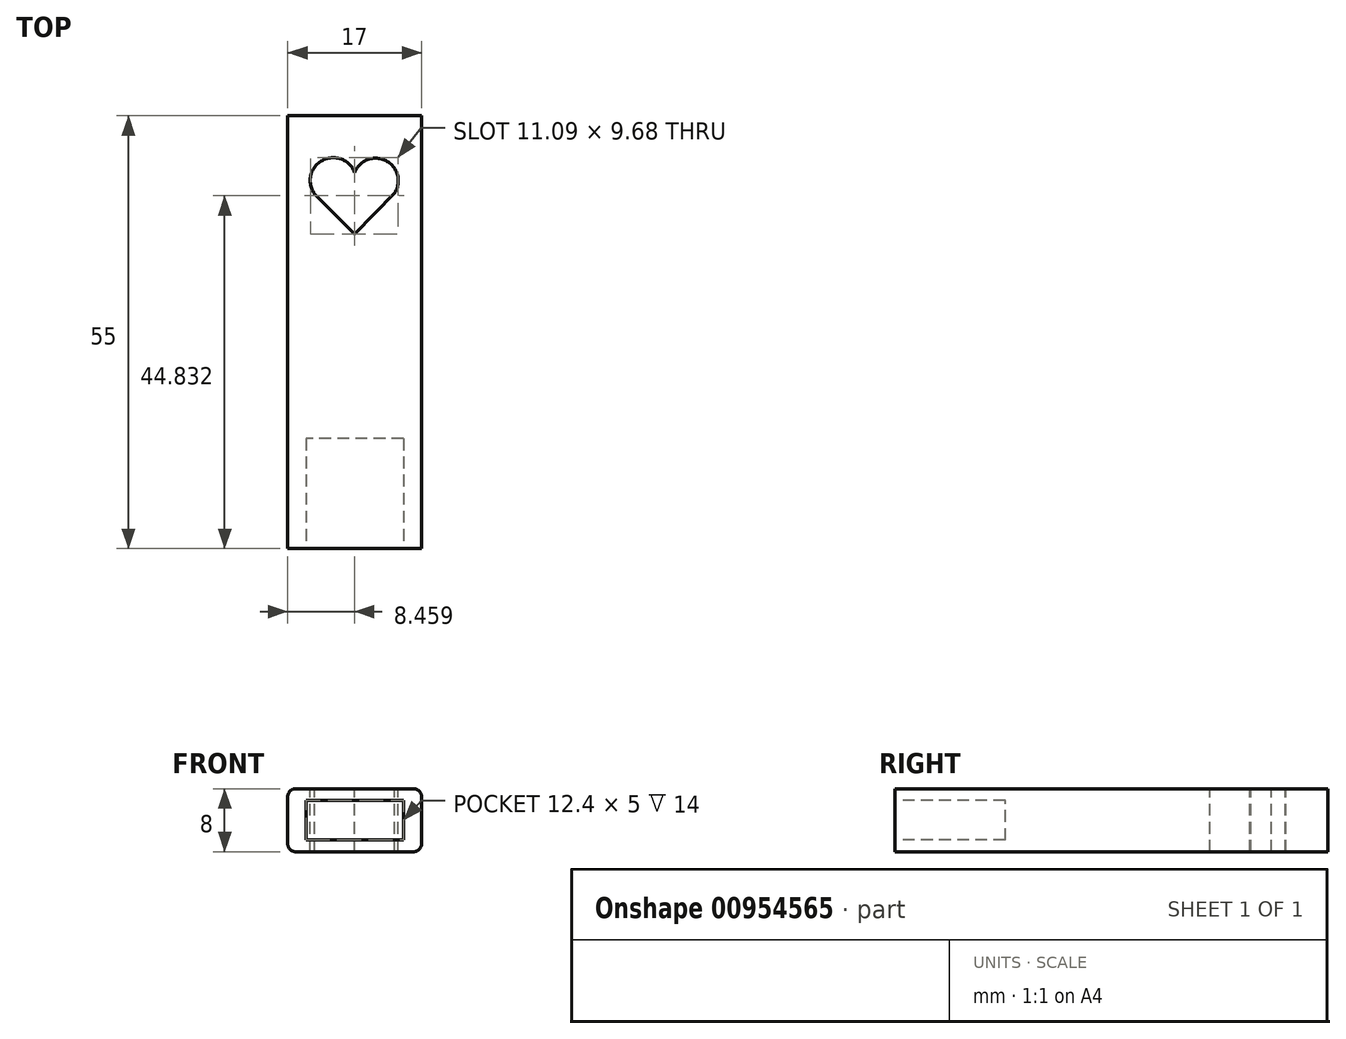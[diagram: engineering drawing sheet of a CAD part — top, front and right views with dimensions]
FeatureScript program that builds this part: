
annotation { "Feature Type Name" : "Feature", "Feature Type Description" : "" }
export const myFeature = defineFeature(function(context is Context, id is Id, definition is map)
    precondition{}
    {
        {
            var Q0;
            Q0=qCreatedBy(makeId("Front.planeOp"),FACE);
            var sketch = newSketch(context, id + "F0", { "sketchPlane" : qUnion([Q0])});
            skLineSegment(sketch, "E0.bottom", {"start": v(8.5, -4) * mm, "end": v(-8.5, -4) * mm});
            skLineSegment(sketch, "E0.top", {"start": v(8.5, 4) * mm, "end": v(-8.5, 4) * mm});
            skLineSegment(sketch, "E0.left", {"start": v(8.5, -4) * mm, "end": v(8.5, 4) * mm});
            skLineSegment(sketch, "E0.right", {"start": v(-8.5, -4) * mm, "end": v(-8.5, 4) * mm});
            skPoint(sketch, "E0.middle", {"position": v(0, 0) * mm});
            skSolve(sketch);
        }
        {
            var Q0;
            Q0 = qSketchRegion(id + "F0", true);
            extrude(context, id + "F1", {"entities" : qUnion([Q0]), "depth" : 55 * mm, "offsetDistance" : 25 * mm});
        }
        {
            var Q0;
            Q0=makeQuery(id+"F1.opExtrude","SWEPT_EDGE",EDGE,{"disambiguationData":[OSD([sQuery(id+"F0.wireOp",EDGE,"E0.top"),sQuery(id+"F0.wireOp",EDGE,"E0.right")])]});
            var Q1;
            Q1=makeQuery(id+"F1.opExtrude","SWEPT_EDGE",EDGE,{"disambiguationData":[OSD([sQuery(id+"F0.wireOp",EDGE,"E0.bottom"),sQuery(id+"F0.wireOp",EDGE,"E0.right")])]});
            var Q2;
            Q2=makeQuery(id+"F1.opExtrude","SWEPT_EDGE",EDGE,{"disambiguationData":[OSD([sQuery(id+"F0.wireOp",EDGE,"E0.bottom"),sQuery(id+"F0.wireOp",EDGE,"E0.left")])]});
            var Q3;
            Q3=makeQuery(id+"F1.opExtrude","SWEPT_EDGE",EDGE,{"disambiguationData":[OSD([sQuery(id+"F0.wireOp",EDGE,"E0.top"),sQuery(id+"F0.wireOp",EDGE,"E0.left")])]});
            fillet(context, id + "F2", {"entities" : qUnion([Q0, Q1, Q2, Q3]), "radius" : 1 * mm, "tangentPropagation" : true, "allowEdgeOverflow" : false});
        }
        {
            var Q0;
            Q0=makeQuery(id+"F1.opExtrude","CAP_FACE",FACE,{"disambiguationData":[OSD([sQuery(id+"F0.wireOp",EDGE,"E0.bottom"),sQuery(id+"F0.wireOp",EDGE,"E0.top"),sQuery(id+"F0.wireOp",EDGE,"E0.left"),sQuery(id+"F0.wireOp",EDGE,"E0.right")])],"isStart":false});
            var sketch = newSketch(context, id + "F3", { "sketchPlane" : qUnion([Q0])});
            skLineSegment(sketch, "E1.bottom", {"start": v(6.2, -2.5) * mm, "end": v(-6.2, -2.5) * mm});
            skLineSegment(sketch, "E1.top", {"start": v(6.2, 2.5) * mm, "end": v(-6.2, 2.5) * mm});
            skLineSegment(sketch, "E1.left", {"start": v(6.2, -2.5) * mm, "end": v(6.2, 2.5) * mm});
            skLineSegment(sketch, "E1.right", {"start": v(-6.2, -2.5) * mm, "end": v(-6.2, 2.5) * mm});
            skPoint(sketch, "E1.middle", {"position": v(0, 0) * mm});
            skSolve(sketch);
        }
        {
            var Q0;
            Q0=makeQuery(id+"F3.imprint","IMPRINT",FACE,{"disambiguationData":[TD([[makeQuery(id+"F3.imprint","IMPRINT",EDGE,{"derivedFrom":sQuery(id+"F3.wireOp",EDGE,"E1.bottom")}),-1.0]])]});
            extrude(context, id + "F4", {"entities" : qUnion([Q0]), "operationType" : NewBodyOperationType.REMOVE, "oppositeDirection" : true, "depth" : 14 * mm, "offsetDistance" : 25 * mm});
        }
        {
            var Q0;
            Q0=makeQuery(id+"F1.opExtrude","SWEPT_FACE",FACE,{"disambiguationData":[OSD([sQuery(id+"F0.wireOp",EDGE,"E0.top")])]});
            var sketch = newSketch(context, id + "F5", { "sketchPlane" : qUnion([Q0])});
            skArc(sketch, "E2", {"start": v(0, -7.22) * mm, "mid": v(-4.1, -5.67) * mm, "end": v(-5.1, -9.94) * mm});
            skArc(sketch, "E3", {"start": v(5.1, -9.8) * mm, "mid": v(3.97, -5.7) * mm, "end": v(0, -7.22) * mm});
            skLineSegment(sketch, "E4", {"start": v(-5.1, -9.94) * mm, "end": v(0, -15) * mm});
            skLineSegment(sketch, "E5", {"start": v(5.1, -9.8) * mm, "end": v(0, -15) * mm});
            skSolve(sketch);
        }
        {
            var Q0;
            Q0=makeQuery(id+"F5.imprint","IMPRINT",FACE,{"disambiguationData":[TD([[makeQuery(id+"F5.imprint","IMPRINT",EDGE,{"derivedFrom":sQuery(id+"F5.wireOp",EDGE,"E2")}),1.0]])]});
            extrude(context, id + "F6", {"entities" : qUnion([Q0]), "operationType" : NewBodyOperationType.REMOVE, "oppositeDirection" : true, "depth" : 25 * mm, "offsetDistance" : 25 * mm});
        }
    });
